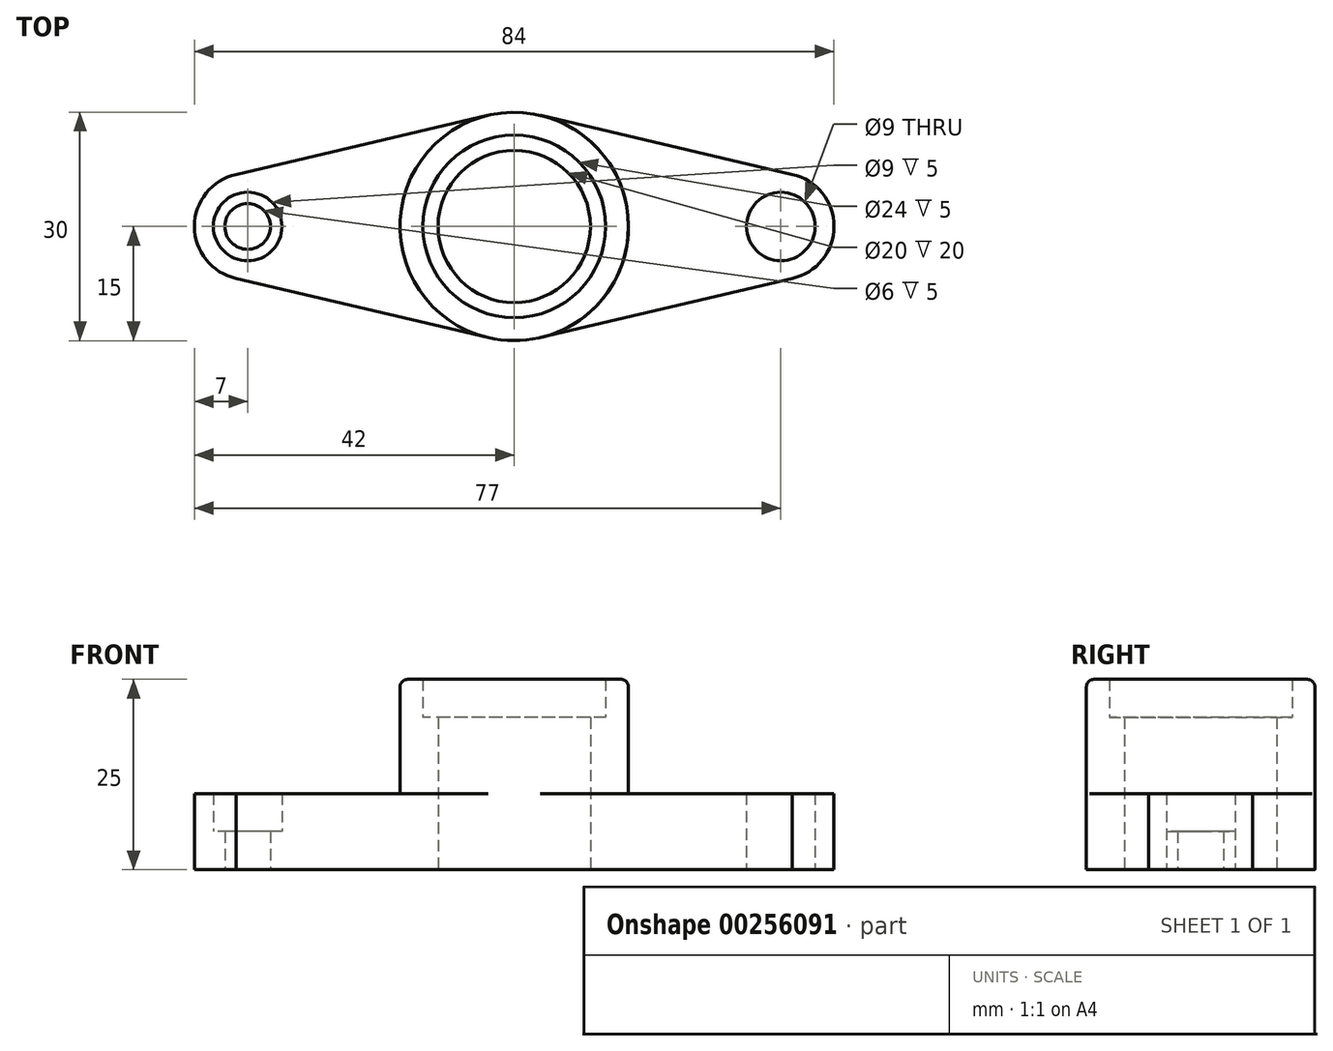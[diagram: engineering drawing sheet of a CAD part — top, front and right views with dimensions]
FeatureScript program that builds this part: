
annotation { "Feature Type Name" : "Feature", "Feature Type Description" : "" }
export const myFeature = defineFeature(function(context is Context, id is Id, definition is map)
    precondition{}
    {
        {
            var Q0;
            Q0=qCreatedBy(makeId("Top.planeOp"),FACE);
            var sketch = newSketch(context, id + "F0", { "sketchPlane" : qUnion([Q0])});
            skLineSegment(sketch, "E0", {"start": v(0, 0) * mm, "end": v(0, -24.21) * mm, "construction": true});
            skLineSegment(sketch, "E1", {"start": v(0, 0) * mm, "end": v(-53.82, 0) * mm, "construction": true});
            skCircle(sketch, "E2", {"center": v(0, 0) * mm, "radius": 15 * mm});
            skCircle(sketch, "E3", {"center": v(0, 0) * mm, "radius": 12 * mm});
            skCircle(sketch, "E4", {"center": v(0, 0) * mm, "radius": 10 * mm});
            skCircle(sketch, "E5", {"center": v(0, 0) * mm, "radius": 35 * mm, "construction": true});
            skCircle(sketch, "E6", {"center": v(-35, 0) * mm, "radius": 4.5 * mm});
            skCircle(sketch, "E7", {"center": v(-35, 0) * mm, "radius": 3 * mm});
            skCircle(sketch, "E8.MirrorC", {"center": v(35, 0) * mm, "radius": 4.5 * mm});
            skCircle(sketch, "E9.MirrorC", {"center": v(35, 0) * mm, "radius": 3 * mm});
            skArc(sketch, "E10", {"start": v(-36.5, 6.84) * mm, "mid": v(-42, 0) * mm, "end": v(-36.5, -6.84) * mm});
            skLineSegment(sketch, "E11", {"start": v(-36.5, -6.84) * mm, "end": v(-3.44, -14.6) * mm});
            skLineSegment(sketch, "E12.MirrorCS", {"start": v(-36.5, 6.84) * mm, "end": v(-3.44, 14.6) * mm});
            skLineSegment(sketch, "E13.MirrorCS", {"start": v(36.5, 6.84) * mm, "end": v(3.44, 14.6) * mm});
            skLineSegment(sketch, "E14.MirrorCS", {"start": v(36.5, -6.84) * mm, "end": v(3.44, -14.6) * mm});
            skArc(sketch, "E15.MirrorC", {"start": v(36.5, 6.84) * mm, "mid": v(42, 0) * mm, "end": v(36.5, -6.84) * mm});
            skSolve(sketch);
        }
        {
            var Q0;
            Q0 = qSketchRegion(id + "F0", true);
            extrude(context, id + "F1", {"entities" : qUnion([Q0]), "depth" : 10 * mm});
        }
        {
            var Q0;
            Q0=makeQuery(id+"F0.imprint","IMPRINT",FACE,{"disambiguationData":[TD([[makeQuery(id+"F0.imprint","IMPRINT",EDGE,{"derivedFrom":sQuery(id+"F0.wireOp",EDGE,"E3")}),-1.0]])]});
            extrude(context, id + "F2", {"entities" : qUnion([Q0]), "depth" : 25 * mm});
        }
        {
            var Q0;
            Q0=makeQuery(id+"F0.imprint","IMPRINT",FACE,{"disambiguationData":[TD([[makeQuery(id+"F0.imprint","IMPRINT",EDGE,{"derivedFrom":sQuery(id+"F0.wireOp",EDGE,"E3")}),1.0]])]});
            extrude(context, id + "F3", {"entities" : qUnion([Q0]), "operationType" : NewBodyOperationType.ADD, "depth" : 20 * mm});
        }
        {
            var Q0;
            Q0=makeQuery(id+"F0.imprint","IMPRINT",FACE,{"disambiguationData":[TD([[makeQuery(id+"F0.imprint","IMPRINT",EDGE,{"derivedFrom":sQuery(id+"F0.wireOp",EDGE,"E6")}),1.0]])]});
            var Q1;
            Q1=makeQuery(id+"F0.imprint","IMPRINT",FACE,{"disambiguationData":[TD([[makeQuery(id+"F0.imprint","IMPRINT",EDGE,{"derivedFrom":sQuery(id+"F0.wireOp",EDGE,"E8.MirrorC")}),-1.0]])]});
            extrude(context, id + "F4", {"entities" : qUnion([Q0, Q1]), "operationType" : NewBodyOperationType.ADD, "depth" : 5 * mm});
        }
        {
            var Q0;
            Q0=makeQuery(id+"F2.opExtrude","CAP_EDGE",EDGE,{"disambiguationData":[OSD([sQuery(id+"F0.wireOp",EDGE,"E2")])],"isStart":false});
            fillet(context, id + "F5", {"entities" : qUnion([Q0]), "radius" : 1 * mm, "tangentPropagation" : true, "allowEdgeOverflow" : false});
        }
    });
